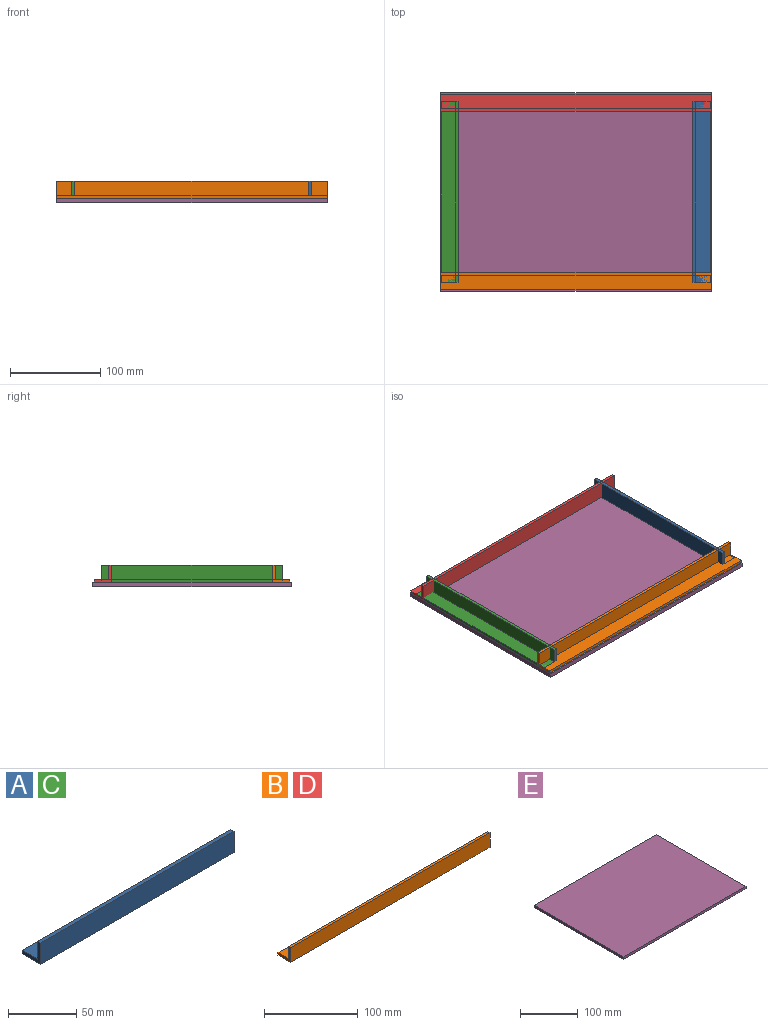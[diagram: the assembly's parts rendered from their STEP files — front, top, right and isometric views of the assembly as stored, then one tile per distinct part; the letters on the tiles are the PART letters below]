
ASSEMBLY  parts=5 mates=4
PART A: 8 faces, bbox 200x19x19 mm
  f0: plane 200x19mm, normal (0,-1,0), area 3800mm2, adj f1,f5,f6,f7
  f1: plane 200x19mm, normal (0,0,-1), area 3800mm2, adj f0,f2,f6,f7
  f2: plane 200x3.17mm, normal (0,1,0), area 634mm2, adj f1,f3,f6,f7
  f3: plane 200x15.83mm, normal (0,0,1), area 3166mm2, adj f2,f4,f6,f7
  f4: plane 200x15.83mm, normal (0,1,0), area 3166mm2, adj f3,f5,f6,f7
  f5: plane 200x3.17mm, normal (0,0,1), area 634mm2, adj f0,f4,f6,f7
  f6: plane 19x19mm, normal (1,0,0), area 110.4mm2, adj f0,f1,f2,f3,f4,f5
  f7: plane 19x19mm, normal (-1,0,0), area 110.4mm2, adj f0,f1,f2,f3,f4,f5
PART B: 8 faces, bbox 300x19x19 mm
  f0: plane 300x19mm, normal (0,-1,0), area 5700mm2, adj f1,f5,f6,f7
  f1: plane 300x19mm, normal (0,0,-1), area 5700mm2, adj f0,f2,f6,f7
  f2: plane 300x3.17mm, normal (0,1,0), area 951mm2, adj f1,f3,f6,f7
  f3: plane 300x15.83mm, normal (0,0,1), area 4749mm2, adj f2,f4,f6,f7
  f4: plane 300x15.83mm, normal (0,1,0), area 4749mm2, adj f3,f5,f6,f7
  f5: plane 300x3.17mm, normal (0,0,1), area 951mm2, adj f0,f4,f6,f7
  f6: plane 19x19mm, normal (1,0,0), area 110.4mm2, adj f0,f1,f2,f3,f4,f5
  f7: plane 19x19mm, normal (-1,0,0), area 110.4mm2, adj f0,f1,f2,f3,f4,f5
PART C: same geometry as A
PART D: same geometry as B
PART E: 6 faces, bbox 300x220x5 mm
  f0: plane 300x5mm, normal (0,-1,0), area 1500mm2, adj f1,f3,f4,f5
  f1: plane 220x5mm, normal (1,0,0), area 1100mm2, adj f0,f2,f4,f5
  f2: plane 300x5mm, normal (0,1,0), area 1500mm2, adj f1,f3,f4,f5
  f3: plane 220x5mm, normal (-1,0,0), area 1100mm2, adj f0,f2,f4,f5
  f4: plane 300x220mm, normal (0,0,1), area 66000mm2, adj f0,f1,f2,f3
  f5: plane 300x220mm, normal (0,0,-1), area 66000mm2, adj f0,f1,f2,f3
PLACE A rot(axis=(0,0,-1),90deg) t=(91.89,-328.28,10.38)mm
PLACE B rot(axis=(0,0,1),180deg) t=(-47.11,-127.28,10.38)mm
PLACE C rot(axis=(0,0,1),90deg) t=(-187.11,271.72,10.38)mm
PLACE D t=(-47.11,70.72,10.38)mm
PLACE E t=(-47.11,-28.28,-4.12)mm fixed
MATE planar B.f1 <-> E.f4  axis (0,0,-1) through (-47.11,-127.28,0.88)mm
MATE planar D.f1 <-> E.f4  axis (0,0,-1) through (-47.11,70.72,0.88)mm
MATE planar C.f1 <-> E.f4  axis (0,0,-1) through (-187.11,-28.28,0.88)mm
MATE planar A.f1 <-> E.f4  axis (0,0,-1) through (91.89,-28.28,0.88)mm
